# Revit family: P400226-031
name_source: partatom
category: Lighting Fixtures
revit_build: Autodesk Revit 2014 (Build: 20130308_1515(x64)
units: mm (PartAtom-declared; Revit-internal decimal feet)

## types (1)
- P400226-031
    Apparent Load = 100 VA
    Assembly Code = D5020200
    Connector Description = Lighting Connector
    Default Elevation = 48"
    Depth = 3 7/8"
    Description = Stick with simple geometric forms and clean crisp lines with this modern
wall bracket. Beautiful opal glass shades visually calm the sharp edges of the
boxy frame in a masterful stroke of design excellence. The frame is coated in
a classic brushed nickel finish that contrasts the light shades. The light fixture
is just right for spaces in need of a subtle, feminine touch.
    Fixture distribution = Direct
    Glass = Paint - Hubbell - White Texture
    Gold = Hubbell - Gold
    Height = 12 7/8"
    Housing Material = Paint - Hubbell - Textured Camera Black
    Lamp = LED or Incandescent
    Load Classification = Lighting
    Manufacturer = Progress Lighting
    Model = P400226-031
    Power Factor = 1
    Product Documentation Link = https://hubbellcdn.com
    Product Link = https://www.hubbell.com
    Specifications = Beautiful opal glass shades visually calm the sharp edges of the boxy frame in a masterful
stroke of design excellence.
• The frame is coated in a classic black finish that contrasts the light shades.
• The light fixture is just right for spaces in need of a subtle, feminine touch.
• Ideal for any foyer, dining room, or kitchen.
• Perfect for transitional, modern, and contemporary settings.
• Measures 21-5/8-inch width by 12-7/8-inch height.
• Uses four medium base bulbs that are sold separately (100w max - LED or incandescent).
• Able to be fully dimmable with dimmable bulbs.
• Includes installation instructions and mounting hardware.
• Progress Lighting products are designed for exceptional quality, reliability, and functionality.
    Square = 21 5/8"
    URL = https://www.hubbell.com
    Voltage = 120 V
    Warranty = 1 year Warranty
    Wattage Comments = 100W
    Watts = 100 W
    White = Paint - Hubbell - Matte White
    Wood = Paint - Hubbell - Textured Camera Black

## geometry (parser evidence)
native form markers: Sweep x4
no freeform markers — native parametric forms only
